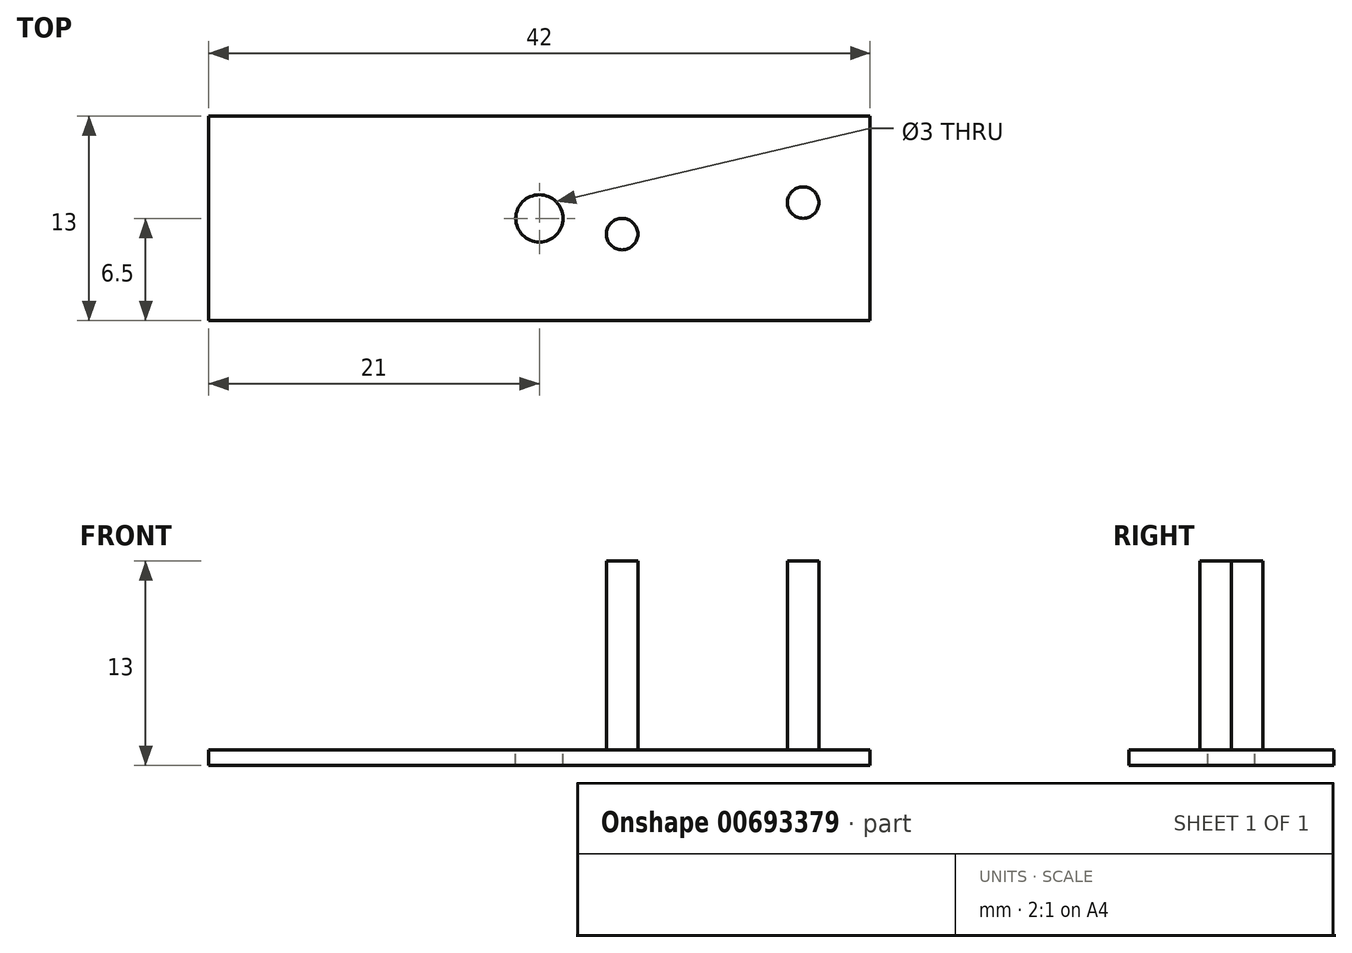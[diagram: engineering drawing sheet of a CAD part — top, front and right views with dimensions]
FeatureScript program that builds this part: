
annotation { "Feature Type Name" : "Feature", "Feature Type Description" : "" }
export const myFeature = defineFeature(function(context is Context, id is Id, definition is map)
    precondition{}
    {
        {
            var Q0;
            Q0=qCreatedBy(makeId("Top.planeOp"),FACE);
            var sketch = newSketch(context, id + "F0", { "sketchPlane" : qUnion([Q0])});
            skLineSegment(sketch, "E0.bottom", {"start": v(-21, 6.5) * mm, "end": v(21, 6.5) * mm});
            skLineSegment(sketch, "E0.top", {"start": v(-21, -6.5) * mm, "end": v(21, -6.5) * mm});
            skLineSegment(sketch, "E0.left", {"start": v(-21, 6.5) * mm, "end": v(-21, -6.5) * mm});
            skLineSegment(sketch, "E0.right", {"start": v(21, 6.5) * mm, "end": v(21, -6.5) * mm});
            skSolve(sketch);
        }
        {
            var Q0;
            Q0=makeQuery(id+"F0.imprint","IMPRINT",FACE,{"disambiguationData":[TD([[makeQuery(id+"F0.imprint","IMPRINT",EDGE,{"derivedFrom":sQuery(id+"F0.wireOp",EDGE,"E0.bottom")}),-1.0]])]});
            extrude(context, id + "F1", {"entities" : qUnion([Q0]), "depth" : 13 * mm, "offsetDistance" : 25 * mm});
        }
        {
            var Q0;
            Q0=makeQuery(id+"F1.opExtrude","CAP_FACE",FACE,{"disambiguationData":[OSD([sQuery(id+"F0.wireOp",EDGE,"E0.bottom"),sQuery(id+"F0.wireOp",EDGE,"E0.top"),sQuery(id+"F0.wireOp",EDGE,"E0.left"),sQuery(id+"F0.wireOp",EDGE,"E0.right")])],"isStart":false});
            var sketch = newSketch(context, id + "F2", { "sketchPlane" : qUnion([Q0])});
            skCircle(sketch, "E1", {"center": v(-16.75, 1) * mm, "radius": 1 * mm});
            skCircle(sketch, "E2", {"center": v(-5.25, -1) * mm, "radius": 1 * mm});
            skCircle(sketch, "E3.MirrorC", {"center": v(16.75, 1) * mm, "radius": 1 * mm});
            skCircle(sketch, "E4.MirrorC", {"center": v(5.25, -1) * mm, "radius": 1 * mm});
            skCircle(sketch, "E5", {"center": v(0, 0) * mm, "radius": 1.5 * mm});
            skSolve(sketch);
        }
        {
            var Q0;
            Q0=makeQuery(id+"F2.imprint","IMPRINT",FACE,{"disambiguationData":[TD([[makeQuery(id+"F2.imprint","IMPRINT",EDGE,{"derivedFrom":sQuery(id+"F2.wireOp",EDGE,"E1")}),1.0]])]});
            var Q1;
            Q1=makeQuery(id+"F2.imprint","IMPRINT",FACE,{"disambiguationData":[TD([[makeQuery(id+"F2.imprint","IMPRINT",EDGE,{"derivedFrom":sQuery(id+"F2.wireOp",EDGE,"E2")}),1.0]])]});
            var Q2;
            Q2=makeQuery(id+"F2.imprint","IMPRINT",FACE,{"disambiguationData":[TD([[makeQuery(id+"F2.imprint","IMPRINT",EDGE,{"derivedFrom":sQuery(id+"F2.wireOp",EDGE,"E4.MirrorC")}),-1.0]])]});
            var Q3;
            Q3=makeQuery(id+"F2.imprint","IMPRINT",FACE,{"disambiguationData":[TD([[makeQuery(id+"F2.imprint","IMPRINT",EDGE,{"derivedFrom":sQuery(id+"F2.wireOp",EDGE,"E3.MirrorC")}),-1.0]])]});
            extrude(context, id + "F3", {"entities" : qUnion([Q0, Q1, Q2, Q3]), "operationType" : NewBodyOperationType.REMOVE, "oppositeDirection" : true, "depth" : 12 * mm, "offsetDistance" : 25 * mm});
        }
        {
            var Q0;
            Q0=makeQuery(id+"F1.opExtrude","CAP_FACE",FACE,{"disambiguationData":[OSD([sQuery(id+"F0.wireOp",EDGE,"E0.bottom"),sQuery(id+"F0.wireOp",EDGE,"E0.top"),sQuery(id+"F0.wireOp",EDGE,"E0.left"),sQuery(id+"F0.wireOp",EDGE,"E0.right")])],"isStart":false});
            var sketch = newSketch(context, id + "F4", { "sketchPlane" : qUnion([Q0])});
            skCircle(sketch, "E6", {"center": v(0, 0) * mm, "radius": 1.5 * mm});
            skSolve(sketch);
        }
        {
            var Q0;
            Q0 = qSketchRegion(id + "F4", true);
            extrude(context, id + "F5", {"entities" : qUnion([Q0]), "operationType" : NewBodyOperationType.REMOVE, "endBound" : BoundingType.THROUGH_ALL, "oppositeDirection" : true, "depth" : 25 * mm, "offsetDistance" : 25 * mm});
        }
    });
